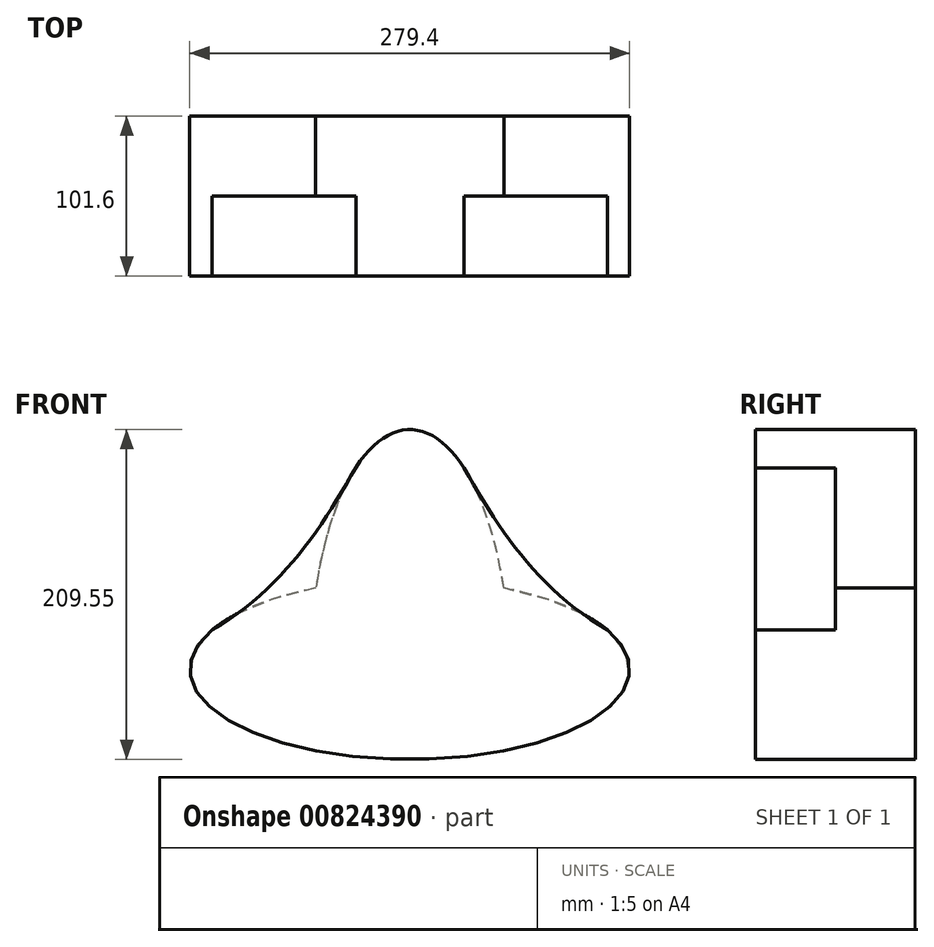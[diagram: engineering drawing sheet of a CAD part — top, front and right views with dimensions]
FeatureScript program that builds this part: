
annotation { "Feature Type Name" : "Feature", "Feature Type Description" : "" }
export const myFeature = defineFeature(function(context is Context, id is Id, definition is map)
    precondition{}
    {
        {
            var Q0;
            Q0=qCreatedBy(makeId("Front.planeOp"),FACE);
            var sketch = newSketch(context, id + "F0", { "sketchPlane" : qUnion([Q0])});
            skEllipse(sketch, "E0", {"center": v(0, 0) * mm, "majorRadius": 152.4 * mm, "minorRadius": 63.5 * mm, "majorAxis": v(0, 1)});
            skEllipse(sketch, "E1", {"center": v(0, 0) * mm, "majorRadius": 139.7 * mm, "minorRadius": 57.15 * mm, "majorAxis": v(1, 0)});
            skSolve(sketch);
        }
        {
            var Q0;
            {var subQ0=sQuery(id+"F0.wireOp",EDGE,"E1");var subQ1=sQuery(id+"F0.wireOp",EDGE,"E0");var subQ2=makeQuery(id+"F0.imprint","INTERSECT",VERTEX,{"disambiguationData":[OD(1.0)],"derivedFrom":[subQ1,subQ0]});Q0=makeQuery(id+"F0.imprint","IMPRINT",FACE,{"disambiguationData":[TD([[makeQuery(id+"F0.imprint","IMPRINT",EDGE,{"disambiguationData":[TD([[subQ2,1.0]])],"derivedFrom":subQ1}),1.0]])]});}
            var Q1;
            {var subQ0=sQuery(id+"F0.wireOp",EDGE,"E1");var subQ1=sQuery(id+"F0.wireOp",EDGE,"E0");var subQ2=makeQuery(id+"F0.imprint","INTERSECT",VERTEX,{"disambiguationData":[OD(0.0)],"derivedFrom":[subQ1,subQ0]});Q1=makeQuery(id+"F0.imprint","IMPRINT",FACE,{"disambiguationData":[TD([[makeQuery(id+"F0.imprint","IMPRINT",EDGE,{"disambiguationData":[TD([[subQ2,1.0]])],"derivedFrom":subQ1}),-1.0]])]});}
            var Q2;
            {var subQ0=sQuery(id+"F0.wireOp",EDGE,"E1");var subQ1=sQuery(id+"F0.wireOp",EDGE,"E0");var subQ2=makeQuery(id+"F0.imprint","INTERSECT",VERTEX,{"disambiguationData":[OD(0.0)],"derivedFrom":[subQ1,subQ0]});Q2=makeQuery(id+"F0.imprint","IMPRINT",FACE,{"disambiguationData":[TD([[makeQuery(id+"F0.imprint","IMPRINT",EDGE,{"disambiguationData":[TD([[subQ2,1.0]])],"derivedFrom":subQ1}),1.0]])]});}
            var Q3;
            {var subQ0=sQuery(id+"F0.wireOp",EDGE,"E1");var subQ1=sQuery(id+"F0.wireOp",EDGE,"E0");var subQ2=makeQuery(id+"F0.imprint","INTERSECT",VERTEX,{"disambiguationData":[OD(2.0)],"derivedFrom":[subQ1,subQ0]});Q3=makeQuery(id+"F0.imprint","IMPRINT",FACE,{"disambiguationData":[TD([[makeQuery(id+"F0.imprint","IMPRINT",EDGE,{"disambiguationData":[TD([[subQ2,-1.0]])],"derivedFrom":subQ1}),-1.0]])]});}
            extrude(context, id + "F1", {"entities" : qUnion([Q0, Q1, Q2, Q3]), "depth" : 50.8 * mm, "offsetDistance" : 25.4 * mm});
        }
        {
            var Q0;
            Q0=makeQuery(id+"F1.opExtrude","CAP_FACE",FACE,{"disambiguationData":[OSD([sQuery(id+"F0.wireOp",EDGE,"E0"),sQuery(id+"F0.wireOp",EDGE,"E1")])],"isStart":false});
            var sketch = newSketch(context, id + "F2", { "sketchPlane" : qUnion([Q0])});
            skFitSpline(sketch, "E2", {"points": [v(-125.5, 25.11) * mm, v(-34.21, 128.39) * mm], "startDerivative": vector(129.05, 74.35) * mm, "endDerivative": vector(68.36, 121.76) * mm});
            skFitSpline(sketch, "E3", {"points": [v(34.57, 127.83) * mm, v(125.44, 25.16) * mm], "startDerivative": vector(68.18, -120.98) * mm, "endDerivative": vector(128.43, -73.98) * mm});
            skSolve(sketch);
        }
        {
            var Q0;
            {var subQ0=sQuery(id+"F2.wireOp",EDGE,"E2");var subQ1=makeQuery(id+"F1.opExtrude","CAP_EDGE",EDGE,{"disambiguationData":[OSD([sQuery(id+"F0.wireOp",EDGE,"E1")])],"isStart":false});var subQ2=makeQuery(id+"F2.imprint","INTERSECT",VERTEX,{"disambiguationData":[OD(1.0)],"derivedFrom":[subQ1,subQ0]});Q0=makeQuery(id+"F2.imprint","IMPRINT",FACE,{"disambiguationData":[TD([[makeQuery(id+"F2.imprint","IMPRINT",EDGE,{"disambiguationData":[TD([[subQ2,-1.0]])],"derivedFrom":subQ0}),-1.0]])]});}
            var Q1;
            {var subQ0=sQuery(id+"F2.wireOp",EDGE,"E3");var subQ1=makeQuery(id+"F1.opExtrude","CAP_EDGE",EDGE,{"disambiguationData":[OSD([sQuery(id+"F0.wireOp",EDGE,"E0")])],"isStart":false});var subQ2=makeQuery(id+"F2.imprint","INTERSECT",VERTEX,{"disambiguationData":[OD(1.0)],"derivedFrom":[subQ1,subQ0]});Q1=makeQuery(id+"F2.imprint","IMPRINT",FACE,{"disambiguationData":[TD([[makeQuery(id+"F2.imprint","IMPRINT",EDGE,{"disambiguationData":[TD([[subQ2,-1.0]])],"derivedFrom":subQ0}),-1.0]])]});}
            var Q2;
            {var subQ4=makeQuery(id+"F1.opExtrude","CAP_EDGE",EDGE,{"disambiguationData":[OSD([sQuery(id+"F0.wireOp",EDGE,"E1")])],"isStart":false});var subQ6=sQuery(id+"F2.wireOp",EDGE,"E2");var subQ12=makeQuery(id+"F2.imprint","INTERSECT",VERTEX,{"disambiguationData":[OD(0.0)],"derivedFrom":[subQ4,subQ6]});Q2=makeQuery(id+"F2.imprint","IMPRINT",FACE,{"disambiguationData":[TD([[makeQuery(id+"F2.imprint","IMPRINT",EDGE,{"disambiguationData":[TD([[subQ12,-1.0]])],"derivedFrom":subQ6}),-1.0]])]});}
            extrude(context, id + "F3", {"entities" : qUnion([Q0, Q1, Q2]), "operationType" : NewBodyOperationType.ADD, "depth" : 50.8 * mm, "offsetDistance" : 25.4 * mm});
        }
    });
